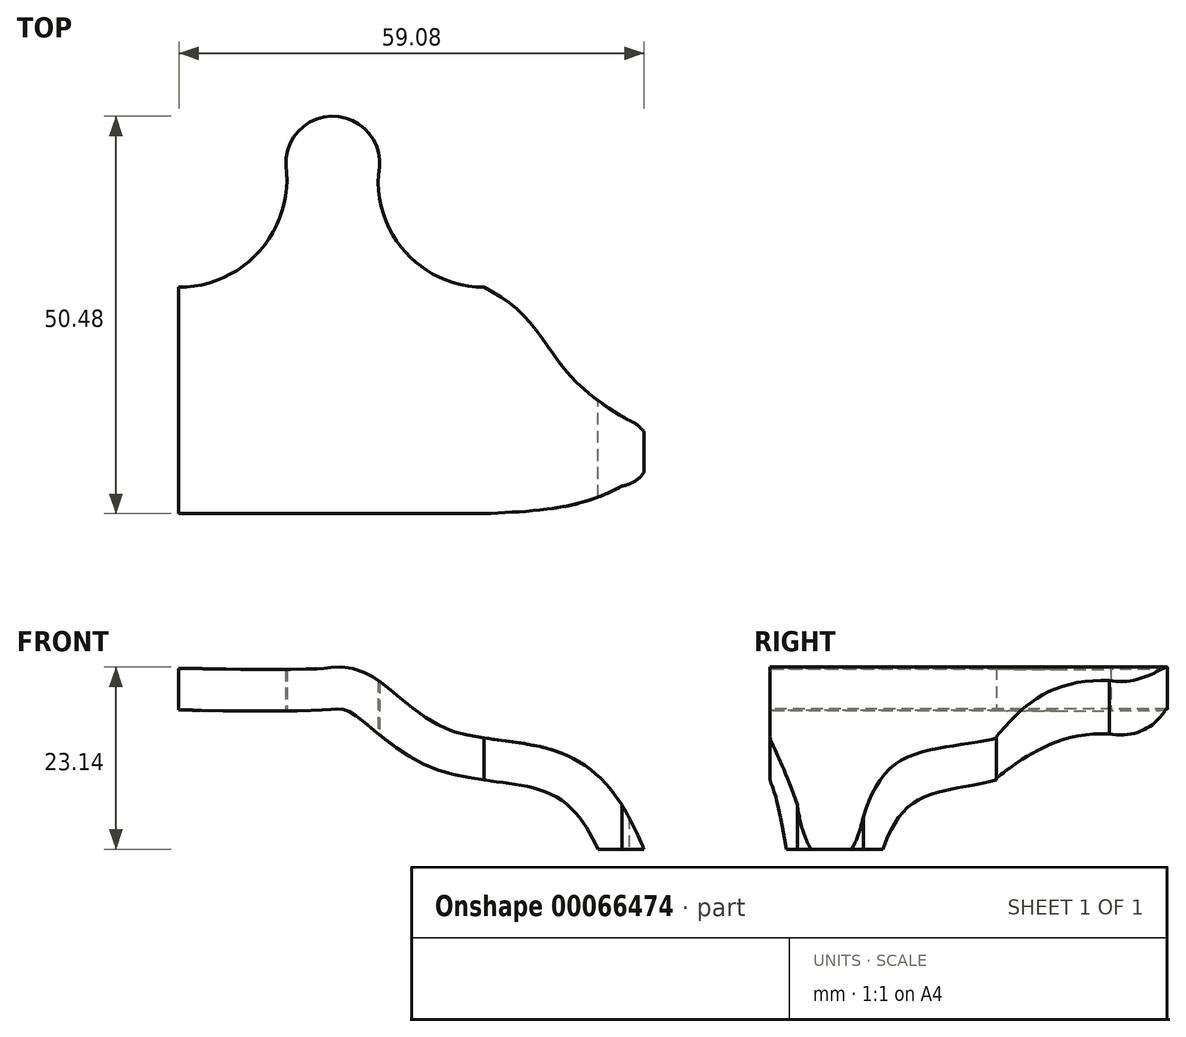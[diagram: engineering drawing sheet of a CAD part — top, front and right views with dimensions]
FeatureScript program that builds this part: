
annotation { "Feature Type Name" : "Feature", "Feature Type Description" : "" }
export const myFeature = defineFeature(function(context is Context, id is Id, definition is map)
    precondition{}
    {
        {
            var Q0;
            Q0=qCreatedBy(makeId("Top.planeOp"),FACE);
            var sketch = newSketch(context, id + "F0", { "sketchPlane" : qUnion([Q0])});
            skLineSegment(sketch, "E0.rect.bottom", {"start": v(-39.14, -8.05) * mm, "end": v(-77.91, -8.05) * mm});
            skLineSegment(sketch, "E0.rect.top", {"start": v(-39.14, -36.8) * mm, "end": v(-77.91, -36.8) * mm});
            skLineSegment(sketch, "E0.rect.left", {"start": v(-39.14, -8.05) * mm, "end": v(-39.14, -36.8) * mm});
            skLineSegment(sketch, "E0.rect.right", {"start": v(-77.91, -8.05) * mm, "end": v(-77.91, -36.8) * mm});
            skPoint(sketch, "E0.rect.middle", {"position": v(-58.52, -22.42) * mm});
            skCircle(sketch, "E1", {"center": v(-22.34, -29) * mm, "radius": 4.36 * mm});
            skCircle(sketch, "E2", {"center": v(-58.36, 7.7) * mm, "radius": 5.97 * mm});
            skArc(sketch, "E3", {"start": v(-52.39, 7.7) * mm, "mid": v(-49.43, -3.26) * mm, "end": v(-39.14, -8.05) * mm});
            skArc(sketch, "E4", {"start": v(-77.91, -8.05) * mm, "mid": v(-67.51, -3.28) * mm, "end": v(-64.33, 7.7) * mm});
            skFitSpline(sketch, "E5", {"points": [v(-21.63, -33.3) * mm, v(-39.14, -36.8) * mm], "startDerivative": vector(-15.64, -8.4) * mm, "endDerivative": vector(-23.89, -1.05) * mm});
            skFitSpline(sketch, "E6", {"points": [v(-20.75, -24.95) * mm, v(-39.14, -8.05) * mm], "startDerivative": vector(-35.95, 20.03) * mm, "endDerivative": vector(-28.05, 14.03) * mm});
            skSolve(sketch);
        }
        {
            var Q0;
            Q0 = qSketchRegion(id + "F0", true);
            extrude(context, id + "F1", {"entities" : qUnion([Q0]), "depth" : 25.4 * mm});
        }
        {
            var Q0;
            Q0=qCreatedBy(makeId("Front.planeOp"),FACE);
            var sketch = newSketch(context, id + "F2", { "sketchPlane" : qUnion([Q0])});
            skFitSpline(sketch, "E7", {"points": [v(-84, 17.83) * mm, v(-59.14, 17.72) * mm, v(-56.24, 17.48) * mm, v(-45.9, 10.4) * mm, v(-30.22, 6.8) * mm, v(-23.36, -2.85) * mm], "startDerivative": vector(111.32, -2.38) * mm, "endDerivative": vector(26.21, -60.24) * mm});
            skFitSpline(sketch, "E8.0", {"points": [v(-83.9, 23.12) * mm, v(-82.73, 23.1) * mm, v(-80.42, 23.05) * mm, v(-77, 22.98) * mm, v(-73.7, 22.92) * mm, v(-70.56, 22.87) * mm, v(-67.64, 22.84) * mm, v(-65, 22.84) * mm, v(-63.1, 22.85) * mm, v(-61.79, 22.88) * mm, v(-60.91, 22.91) * mm, v(-60.3, 22.94) * mm, v(-59.87, 22.97) * mm, v(-59.65, 22.99) * mm, v(-59.49, 23) * mm, v(-59.32, 23.01) * mm, v(-59.1, 23.04) * mm, v(-58.82, 23.07) * mm, v(-58.37, 23.1) * mm, v(-57.8, 23.14) * mm, v(-57.07, 23.12) * mm, v(-56.26, 23.04) * mm, v(-55.37, 22.85) * mm, v(-54.54, 22.54) * mm, v(-53.96, 22.27) * mm, v(-53.44, 21.99) * mm, v(-52.98, 21.7) * mm, v(-52.55, 21.42) * mm, v(-52.03, 21.04) * mm, v(-51.4, 20.56) * mm, v(-50.68, 19.97) * mm, v(-49.95, 19.37) * mm, v(-48.97, 18.56) * mm, v(-47.71, 17.56) * mm, v(-46.42, 16.65) * mm, v(-45.4, 16.03) * mm, v(-44.77, 15.7) * mm, v(-44.27, 15.46) * mm, v(-43.91, 15.3) * mm, v(-43.55, 15.16) * mm, v(-43.04, 14.98) * mm, v(-42.35, 14.77) * mm, v(-41.14, 14.48) * mm, v(-39.48, 14.18) * mm, v(-37.27, 13.88) * mm, v(-35.31, 13.63) * mm, v(-33.68, 13.37) * mm, v(-32.42, 13.12) * mm, v(-31.13, 12.8) * mm, v(-29.82, 12.4) * mm, v(-28.7, 11.95) * mm, v(-27.8, 11.52) * mm, v(-26.92, 11.02) * mm, v(-25.9, 10.34) * mm, v(-24.8, 9.42) * mm, v(-23.81, 8.45) * mm, v(-22.65, 7.1) * mm, v(-21.46, 5.34) * mm, v(-20.3, 3.24) * mm, v(-19.35, 1.2) * mm, v(-18.78, -0.1) * mm, v(-18.5, -0.74) * mm]});
            skLineSegment(sketch, "E9.rect.bottom", {"start": v(-16.47, -0.74) * mm, "end": v(-83.5, -0.74) * mm});
            skLineSegment(sketch, "E9.rect.top", {"start": v(-16.47, 29.9) * mm, "end": v(-83.5, 29.9) * mm});
            skLineSegment(sketch, "E9.rect.left", {"start": v(-16.47, -0.74) * mm, "end": v(-16.47, 29.9) * mm});
            skLineSegment(sketch, "E9.rect.right", {"start": v(-83.5, -0.74) * mm, "end": v(-83.5, 29.9) * mm});
            skPoint(sketch, "E9.rect.middle", {"position": v(-50, 14.58) * mm});
            skSolve(sketch);
        }
        {
            var Q0;
            {var subQ0=sQuery(id+"F2.wireOp",EDGE,"E9.rect.bottom");var subQ1=sQuery(id+"F2.wireOp",EDGE,"E7");var subQ2=makeQuery(id+"F2.imprint","INTERSECT",VERTEX,{"derivedFrom":[subQ1,subQ0]});Q0=makeQuery(id+"F2.imprint","IMPRINT",FACE,{"disambiguationData":[TD([[makeQuery(id+"F2.imprint","IMPRINT",EDGE,{"disambiguationData":[TD([[subQ2,1.0]])],"derivedFrom":subQ1}),1.0]])]});}
            extrude(context, id + "F3", {"entities" : qUnion([Q0]), "operationType" : NewBodyOperationType.INTERSECT, "endBound" : BoundingType.SYMMETRIC, "depth" : 104.66 * mm});
        }
    });
